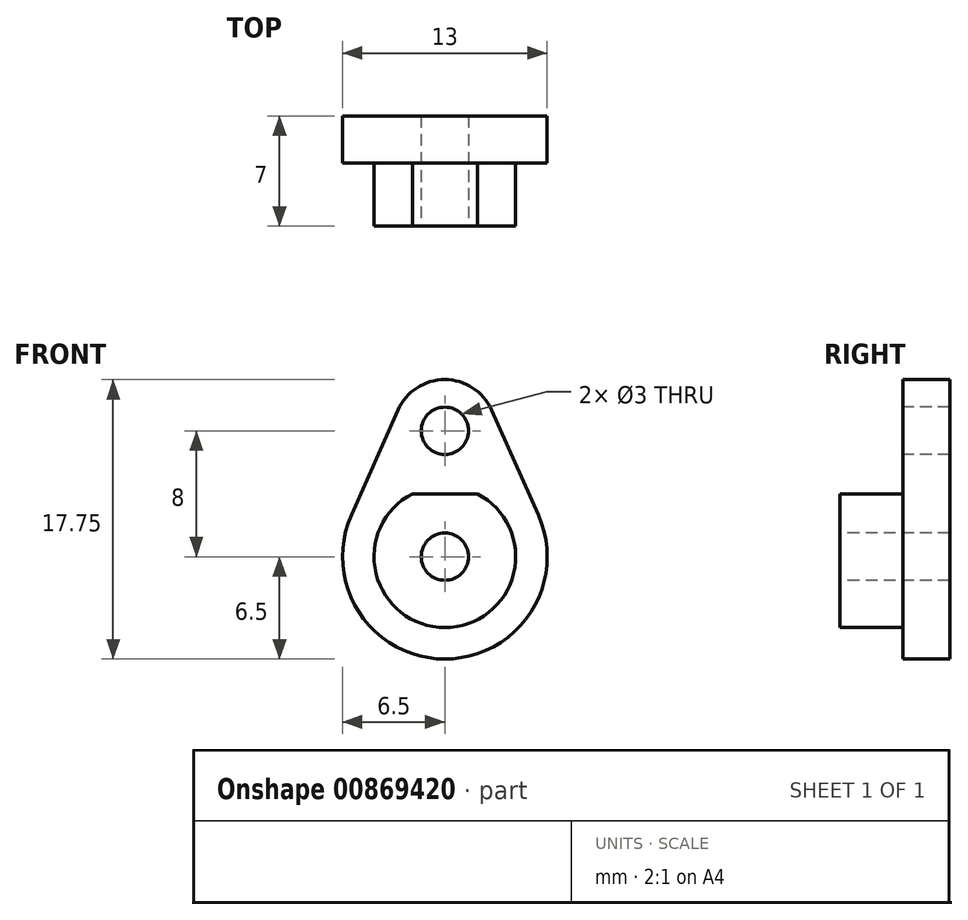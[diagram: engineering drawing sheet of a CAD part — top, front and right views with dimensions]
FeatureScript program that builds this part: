
annotation { "Feature Type Name" : "Feature", "Feature Type Description" : "" }
export const myFeature = defineFeature(function(context is Context, id is Id, definition is map)
    precondition{}
    {
        {
            var Q0;
            Q0=qCreatedBy(makeId("Front.planeOp"),FACE);
            var sketch = newSketch(context, id + "F0", { "sketchPlane" : qUnion([Q0])});
            skArc(sketch, "E0", {"start": v(2.97, 9.32) * mm, "mid": v(0, 11.25) * mm, "end": v(-2.97, 9.32) * mm});
            skCircle(sketch, "E1", {"center": v(0, 0) * mm, "radius": 1.5 * mm, "construction": true});
            skArc(sketch, "E2", {"start": v(-5.94, 2.64) * mm, "mid": v(0, -6.5) * mm, "end": v(5.94, 2.64) * mm});
            skLineSegment(sketch, "E3", {"start": v(-2.97, 9.32) * mm, "end": v(-5.94, 2.64) * mm});
            skLineSegment(sketch, "E4", {"start": v(2.97, 9.32) * mm, "end": v(5.94, 2.64) * mm});
            skCircle(sketch, "E5", {"center": v(0, 8) * mm, "radius": 1.5 * mm});
            skSolve(sketch);
        }
        {
            var Q0;
            Q0=makeQuery(id+"F0.imprint","IMPRINT",FACE,{"disambiguationData":[TD([[makeQuery(id+"F0.imprint","IMPRINT",EDGE,{"derivedFrom":sQuery(id+"F0.wireOp",EDGE,"E0")}),1.0]])]});
            extrude(context, id + "F1", {"entities" : qUnion([Q0]), "oppositeDirection" : true, "depth" : 3 * mm, "offsetDistance" : 25 * mm});
        }
        {
            var Q0;
            Q0=makeQuery(id+"F1.opExtrude","CAP_FACE",FACE,{"disambiguationData":[OSD([sQuery(id+"F0.wireOp",EDGE,"E0"),sQuery(id+"F0.wireOp",EDGE,"E2"),sQuery(id+"F0.wireOp",EDGE,"E3"),sQuery(id+"F0.wireOp",EDGE,"E4"),sQuery(id+"F0.wireOp",EDGE,"E5")])],"isStart":true});
            var sketch = newSketch(context, id + "F2", { "sketchPlane" : qUnion([Q0])});
            skCircle(sketch, "E6", {"center": v(0, 0) * mm, "radius": 4.5 * mm});
            skLineSegment(sketch, "E7", {"start": v(-2.06, 4) * mm, "end": v(2.06, 4) * mm});
            skSolve(sketch);
        }
        {
            var Q0;
            {var subQ0=sQuery(id+"F2.wireOp",EDGE,"E7");Q0=makeQuery(id+"F2.imprint","IMPRINT",FACE,{"disambiguationData":[TD([[makeQuery(id+"F2.imprint","IMPRINT",EDGE,{"derivedFrom":subQ0}),-1.0]])]});}
            extrude(context, id + "F3", {"entities" : qUnion([Q0]), "operationType" : NewBodyOperationType.ADD, "depth" : 4 * mm, "offsetDistance" : 25 * mm});
        }
        {
            var Q0;
            Q0=makeQuery(id+"F3.opExtrude","CAP_FACE",FACE,{"disambiguationData":[OSD([sQuery(id+"F2.wireOp",EDGE,"E6")])],"isStart":false});
            var sketch = newSketch(context, id + "F4", { "sketchPlane" : qUnion([Q0])});
            skCircle(sketch, "E8", {"center": v(0, 0) * mm, "radius": 1.5 * mm});
            skSolve(sketch);
        }
        {
            var Q0;
            Q0=makeQuery(id+"F4.imprint","IMPRINT",FACE,{"disambiguationData":[TD([[makeQuery(id+"F4.imprint","IMPRINT",EDGE,{"derivedFrom":sQuery(id+"F4.wireOp",EDGE,"E8")}),1.0]])]});
            extrude(context, id + "F5", {"entities" : qUnion([Q0]), "operationType" : NewBodyOperationType.REMOVE, "oppositeDirection" : true, "depth" : 20 * mm, "offsetDistance" : 25 * mm});
        }
    });
